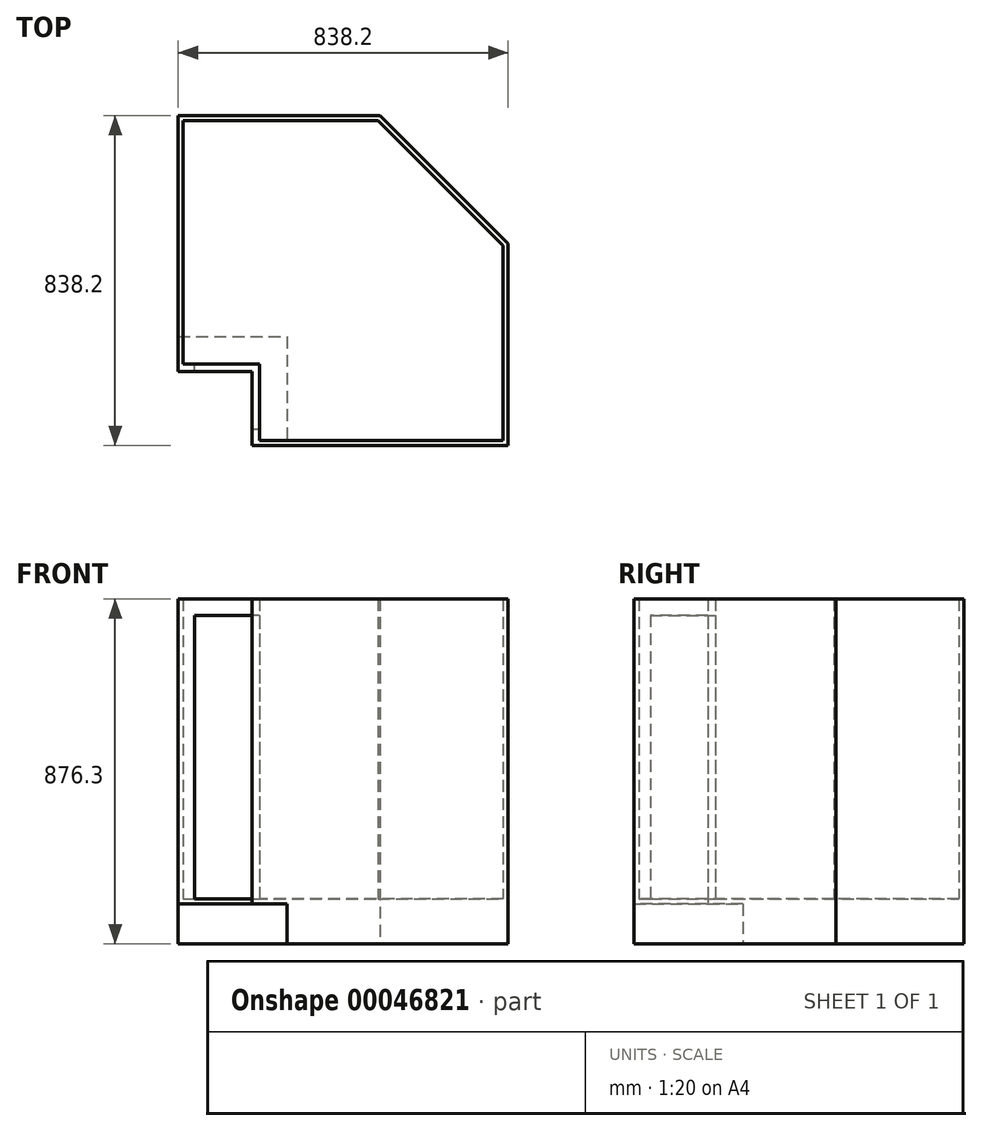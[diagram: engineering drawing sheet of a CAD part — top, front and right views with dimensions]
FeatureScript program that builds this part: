
annotation { "Feature Type Name" : "Feature", "Feature Type Description" : "" }
export const myFeature = defineFeature(function(context is Context, id is Id, definition is map)
    precondition{}
    {
        {
            var Q0;
            Q0=qCreatedBy(makeId("Top.planeOp"),FACE);
            var sketch = newSketch(context, id + "F0", { "sketchPlane" : qUnion([Q0])});
            skLineSegment(sketch, "E0.bottom", {"start": v(-419.1, 419.1) * mm, "end": v(419.1, 419.1) * mm, "construction": true});
            skLineSegment(sketch, "E0.top", {"start": v(-419.1, -419.1) * mm, "end": v(419.1, -419.1) * mm, "construction": true});
            skLineSegment(sketch, "E0.left", {"start": v(-419.1, 419.1) * mm, "end": v(-419.1, -419.1) * mm, "construction": true});
            skLineSegment(sketch, "E0.right", {"start": v(419.1, 419.1) * mm, "end": v(419.1, -419.1) * mm, "construction": true});
            skLineSegment(sketch, "E1", {"start": v(-419.1, 419.1) * mm, "end": v(419.1, -419.1) * mm, "construction": true});
            skLineSegment(sketch, "E2", {"start": v(-419.1, -231.64) * mm, "end": v(-231.64, -419.1) * mm, "construction": true});
            skLineSegment(sketch, "E3", {"start": v(93.57, 419.1) * mm, "end": v(419.1, 93.57) * mm, "construction": true});
            skSolve(sketch);
        }
        {
            var Q0;
            Q0=qCreatedBy(makeId("Top.planeOp"),FACE);
            var sketch = newSketch(context, id + "F1", { "sketchPlane" : qUnion([Q0])});
            skLineSegment(sketch, "E4", {"start": v(-419.1, -231.64) * mm, "end": v(-419.1, 419.1) * mm});
            skLineSegment(sketch, "E5", {"start": v(-231.64, -419.1) * mm, "end": v(419.1, -419.1) * mm});
            skLineSegment(sketch, "E6", {"start": v(419.1, -419.1) * mm, "end": v(419.1, 93.57) * mm});
            skLineSegment(sketch, "E7", {"start": v(-419.1, 419.1) * mm, "end": v(93.57, 419.1) * mm});
            skLineSegment(sketch, "E8", {"start": v(93.57, 419.1) * mm, "end": v(419.1, 93.57) * mm});
            skLineSegment(sketch, "E9", {"start": v(-406.4, -212.59) * mm, "end": v(-406.4, 406.4) * mm});
            skLineSegment(sketch, "E10", {"start": v(-406.4, 406.4) * mm, "end": v(88.3, 406.4) * mm});
            skLineSegment(sketch, "E11", {"start": v(88.3, 406.4) * mm, "end": v(406.4, 88.3) * mm});
            skLineSegment(sketch, "E12", {"start": v(406.4, 88.3) * mm, "end": v(406.4, -406.4) * mm});
            skLineSegment(sketch, "E13", {"start": v(406.4, -406.4) * mm, "end": v(-212.59, -406.4) * mm});
            skLineSegment(sketch, "E14", {"start": v(-419.1, -231.64) * mm, "end": v(-231.64, -231.64) * mm});
            skLineSegment(sketch, "E15", {"start": v(-231.64, -419.1) * mm, "end": v(-231.64, -231.64) * mm});
            skLineSegment(sketch, "E16", {"start": v(-406.4, -212.59) * mm, "end": v(-212.59, -212.59) * mm});
            skLineSegment(sketch, "E17", {"start": v(-212.59, -406.4) * mm, "end": v(-212.59, -212.59) * mm});
            skSolve(sketch);
        }
        {
            var Q0;
            Q0=makeQuery(id+"F1.imprint","IMPRINT",FACE,{"disambiguationData":[TD([[makeQuery(id+"F1.imprint","IMPRINT",EDGE,{"derivedFrom":sQuery(id+"F1.wireOp",EDGE,"e798ca29-4278-4ced-b8ca-b78b60aa5f68")}),1.0]])]});
            var Q1;
            {var subQ1=sQuery(id+"F1.wireOp",EDGE,"E4");Q1=makeQuery(id+"F1.imprint","IMPRINT",FACE,{"disambiguationData":[TD([[makeQuery(id+"F1.imprint","IMPRINT",EDGE,{"derivedFrom":subQ1}),-1.0]])]});}
            extrude(context, id + "F2", {"entities" : qUnion([Q0, Q1]), "depth" : 774.7 * mm});
        }
        {
            var Q0;
            Q0=makeQuery(id+"F2.opExtrude","CAP_FACE",FACE,{"disambiguationData":[OSD([sQuery(id+"F1.wireOp",EDGE,"e798ca29-4278-4ced-b8ca-b78b60aa5f68"),sQuery(id+"F1.wireOp",EDGE,"9b252cdc-31d7-4699-a694-69d285789418"),sQuery(id+"F1.wireOp",EDGE,"4f0292b0-5f3a-4f56-a47e-b266dc19c777"),sQuery(id+"F1.wireOp",EDGE,"d769d018-4a0f-4c55-b41c-e0d83248ed80"),sQuery(id+"F1.wireOp",EDGE,"E4"),sQuery(id+"F1.wireOp",EDGE,"E5"),sQuery(id+"F1.wireOp",EDGE,"E6"),sQuery(id+"F1.wireOp",EDGE,"E7"),sQuery(id+"F1.wireOp",EDGE,"E8"),sQuery(id+"F1.wireOp",EDGE,"E9"),sQuery(id+"F1.wireOp",EDGE,"E10"),sQuery(id+"F1.wireOp",EDGE,"E11"),sQuery(id+"F1.wireOp",EDGE,"E12"),sQuery(id+"F1.wireOp",EDGE,"E13")])],"isStart":true});
            var Q1;
            {var subQ0=sQuery(id+"F1.wireOp",EDGE,"E9");Q1=makeQuery(id+"F1.imprint","IMPRINT",FACE,{"disambiguationData":[TD([[makeQuery(id+"F1.imprint","IMPRINT",EDGE,{"derivedFrom":subQ0}),-1.0]])]});}
            var Q2;
            Q2=sQuery(id+"F1.wireOp",EDGE,"e798ca29-4278-4ced-b8ca-b78b60aa5f68");
            var Q3;
            Q3=sQuery(id+"F1.wireOp",EDGE,"4f0292b0-5f3a-4f56-a47e-b266dc19c777");
            var Q4;
            Q4=sQuery(id+"F1.wireOp",EDGE,"E5");
            var Q5;
            Q5=sQuery(id+"F1.wireOp",EDGE,"9b252cdc-31d7-4699-a694-69d285789418");
            var Q6;
            Q6=sQuery(id+"F1.wireOp",EDGE,"E4");
            var Q7;
            Q7=sQuery(id+"F1.wireOp",EDGE,"E7");
            var Q8;
            Q8=sQuery(id+"F1.wireOp",EDGE,"E8");
            var Q9;
            Q9=sQuery(id+"F1.wireOp",EDGE,"E6");
            extrude(context, id + "F3", {"entities" : qUnion([Q0, Q1]), "operationType" : NewBodyOperationType.ADD, "surfaceEntities" : qUnion([Q2, Q3, Q4, Q5, Q6, Q7, Q8, Q9]), "depth" : 101.6 * mm, "hasSecondDirection" : true, "secondDirectionOppositeDirection" : true, "secondDirectionDepth" : 12.7 * mm});
        }
        {
            var Q0;
            {var subQ0=sQuery(id+"F1.wireOp",EDGE,"E13");var subQ1=sQuery(id+"F1.wireOp",EDGE,"E12");var subQ2=sQuery(id+"F1.wireOp",EDGE,"E11");var subQ3=sQuery(id+"F1.wireOp",EDGE,"E10");var subQ4=sQuery(id+"F1.wireOp",EDGE,"E9");var subQ5=sQuery(id+"F1.wireOp",EDGE,"d769d018-4a0f-4c55-b41c-e0d83248ed80");Q0=makeQuery(id+"F3.boolean.opBoolean","MERGE",FACE,{"derivedFrom":[makeQuery(id+"F3.opExtrude","CAP_FACE",FACE,{"disambiguationData":[OSD([subQ5,subQ4,subQ3,subQ2,subQ1,subQ0])],"isStart":false}),makeQuery(id+"F3.opExtrude","CAP_FACE",FACE,{"disambiguationData":[OSD([sQuery(id+"F1.wireOp",EDGE,"e798ca29-4278-4ced-b8ca-b78b60aa5f68"),sQuery(id+"F1.wireOp",EDGE,"9b252cdc-31d7-4699-a694-69d285789418"),sQuery(id+"F1.wireOp",EDGE,"4f0292b0-5f3a-4f56-a47e-b266dc19c777"),subQ5,sQuery(id+"F1.wireOp",EDGE,"E4"),sQuery(id+"F1.wireOp",EDGE,"E5"),sQuery(id+"F1.wireOp",EDGE,"E6"),sQuery(id+"F1.wireOp",EDGE,"E7"),sQuery(id+"F1.wireOp",EDGE,"E8"),subQ4,subQ3,subQ2,subQ1,subQ0])],"isStart":false})]});}
            var sketch = newSketch(context, id + "F4", { "sketchPlane" : qUnion([Q0])});
            skLineSegment(sketch, "E18", {"start": v(-419.1, 231.64) * mm, "end": v(-419.1, 142.74) * mm});
            skLineSegment(sketch, "E19", {"start": v(-231.64, 419.1) * mm, "end": v(-142.74, 419.1) * mm});
            skLineSegment(sketch, "E20", {"start": v(-419.1, 142.74) * mm, "end": v(-142.74, 142.74) * mm});
            skLineSegment(sketch, "E21", {"start": v(-142.74, 142.74) * mm, "end": v(-142.74, 419.1) * mm});
            skSolve(sketch);
        }
        {
            var Q0;
            Q0=qSketchRegion(id+"F4",true);
            var Q1;
            Q1=makeQuery(id+"F4.imprint","IMPRINT",FACE,{"disambiguationData":[TD([[makeQuery(id+"F4.imprint","IMPRINT",EDGE,{"derivedFrom":sQuery(id+"F4.wireOp",EDGE,"E18")}),1.0]])]});
            extrude(context, id + "F5", {"entities" : qUnion([Q0, Q1]), "operationType" : NewBodyOperationType.REMOVE, "oppositeDirection" : true, "depth" : 101.6 * mm});
        }
        {
            var Q0;
            Q0=makeQuery(id+"F2.opExtrude","SWEPT_FACE",FACE,{"disambiguationData":[OSD([sQuery(id+"F1.wireOp",EDGE,"E16")])]});
            var sketch = newSketch(context, id + "F6", { "sketchPlane" : qUnion([Q0])});
            skLineSegment(sketch, "E22.bottom", {"start": v(212.59, 733.42) * mm, "end": v(377.83, 733.42) * mm});
            skLineSegment(sketch, "E22.top", {"start": v(212.59, 12.7) * mm, "end": v(377.83, 12.7) * mm});
            skLineSegment(sketch, "E22.left", {"start": v(212.59, 733.42) * mm, "end": v(212.59, 12.7) * mm});
            skLineSegment(sketch, "E22.right", {"start": v(377.83, 733.42) * mm, "end": v(377.83, 12.7) * mm});
            skLineSegment(sketch, "E23", {"start": v(377.83, 733.42) * mm, "end": v(419.1, 733.42) * mm, "construction": true});
            skSolve(sketch);
        }
        {
            var Q0;
            Q0=makeQuery(id+"F6.imprint","IMPRINT",FACE,{"disambiguationData":[TD([[makeQuery(id+"F6.imprint","IMPRINT",EDGE,{"derivedFrom":sQuery(id+"F6.wireOp",EDGE,"E22.bottom")}),-1.0]])]});
            extrude(context, id + "F7", {"entities" : qUnion([Q0]), "operationType" : NewBodyOperationType.REMOVE, "oppositeDirection" : true, "depth" : 165.24 * mm});
        }
    });
